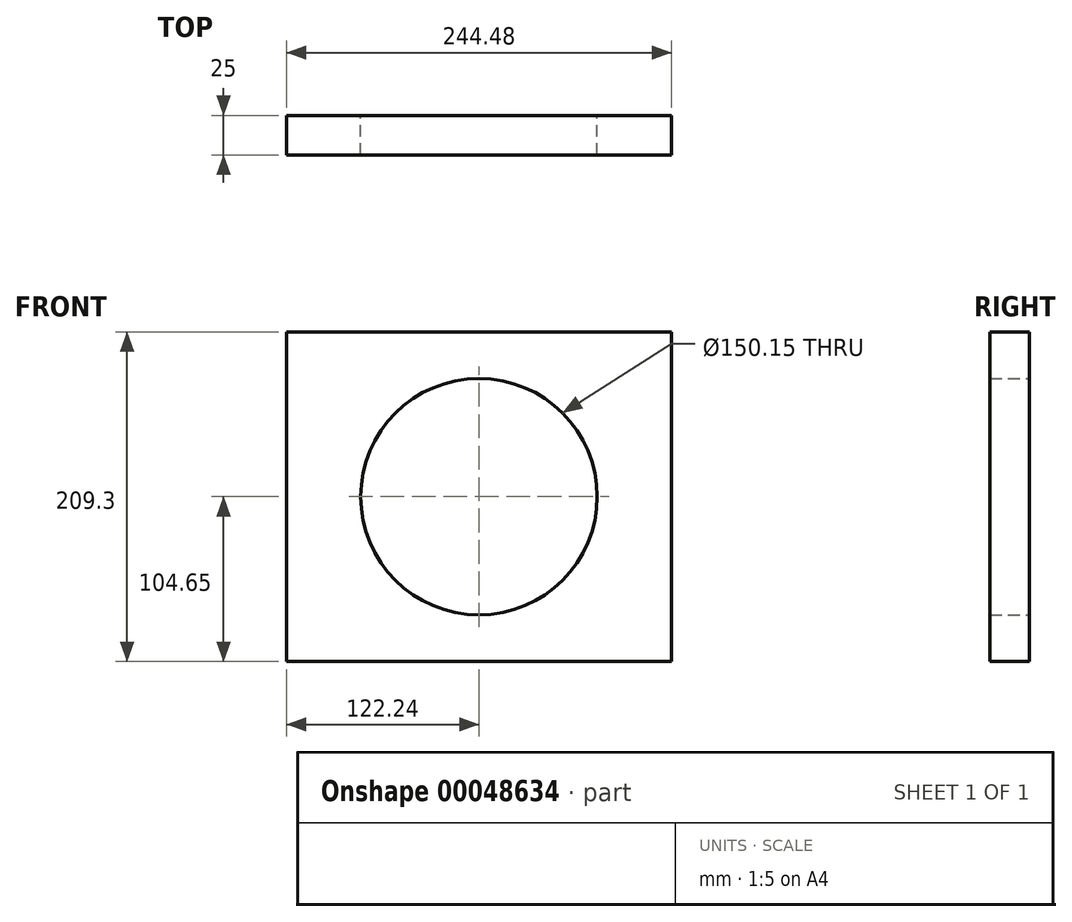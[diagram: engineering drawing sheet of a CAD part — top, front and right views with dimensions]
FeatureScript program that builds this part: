
annotation { "Feature Type Name" : "Feature", "Feature Type Description" : "" }
export const myFeature = defineFeature(function(context is Context, id is Id, definition is map)
    precondition{}
    {
        {
            var Q0;
            Q0=qCreatedBy(makeId("Front.planeOp"),FACE);
            var sketch = newSketch(context, id + "F0", { "sketchPlane" : qUnion([Q0])});
            skLineSegment(sketch, "E0.rect.bottom", {"start": v(-122.24, 104.65) * mm, "end": v(122.24, 104.65) * mm});
            skLineSegment(sketch, "E0.rect.top", {"start": v(-122.24, -104.65) * mm, "end": v(122.24, -104.65) * mm});
            skLineSegment(sketch, "E0.rect.left", {"start": v(-122.24, 104.65) * mm, "end": v(-122.24, -104.65) * mm});
            skLineSegment(sketch, "E0.rect.right", {"start": v(122.24, 104.65) * mm, "end": v(122.24, -104.65) * mm});
            skPoint(sketch, "E0.rect.middle", {"position": v(0, 0) * mm});
            skCircle(sketch, "E1", {"center": v(0, 0) * mm, "radius": 75.08 * mm});
            skSolve(sketch);
        }
        {
            var Q0;
            Q0 = qSketchRegion(id + "F0", true);
            extrude(context, id + "F1", {"entities" : qUnion([Q0]), "depth" : 25 * mm});
        }
    });
